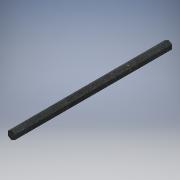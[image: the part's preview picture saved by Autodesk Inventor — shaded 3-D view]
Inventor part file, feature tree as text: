
AUTODESK INVENTOR PART (.ipt)
format: ipt  version: 2016 (Build 200138000, 138)  size: 97,280 bytes
history: native  units: in
note: dims shown in document units (in); Inventor stores cm internally (conversion verified against a paired STEP export)
features: extrude x1, sketch x1
ambient origin geometry x8: Origin, YZ Plane, XZ Plane, XY Plane, X Axis, Y Axis, Z Axis, Center Point
bodies: Solid1 (feature_tree)
feature tree (2):
  extrude  "Extrusion1"  Depth=8.0in TaperAngle=0.0deg
  sketch  "Sketch1"  dims[d0=0.375in d1=8.0in d2=0.0in]
